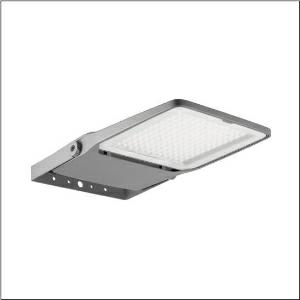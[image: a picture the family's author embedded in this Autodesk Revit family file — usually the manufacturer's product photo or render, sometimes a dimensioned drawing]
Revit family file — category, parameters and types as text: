
# Revit family: floodlight_fl_20_midi___rs17_5xa7682d3b2ac_ca3f
name_source: partatom
category: Lighting Fixtures
units: mm (PartAtom-declared; Revit-internal decimal feet)

## family parameters
Cut with Voids When Loaded = No
Host = Face
Light Source = No
Part Type = Normal
Room Calculation Point = No
Round Connector Dimension = Use Diameter
Shared = No

## types (1)
- --- (1 x LED 5000K / CRI = 70 (unbekannt), 19830 lm, 5000K)
    Apparent Load = 142 VA
    CIE Flux Codes = 79 92 99 100 100
    Color Rendering = 70
    Color Temperature = 5000K
    Default Elevation = 1800 mm
    Description = Floodlight FL 20 midi, floodlight, primary light control with lens, of plastic, primary optical cover: protective disc, of toughened safety glass, transparent, light distribution: RS17, light emission: direct distribution, primary light characteristic: rotationally symmetric, installation type: surface-mounted, LED High Power LED, rated luminous flux: 19.830 lm, light colour: 750, colour temperature: 5000K, control gear: ECG Plus, control: flexible luminous flux parameterisation, time-dependent luminous flux control, digital communication interface, power reduction, overheat protection, electronic power reduction, with terminal, 5-pole, max. 2.5mm², mains connection: 220..240V, AC, 50/60Hz, rated input power: 142W, LED unit, of diecast aluminium, powder-coated, Siteco® metallic grey (DB 702S), length: 731 mm, width: 450 mm, height: 76mm, housing frame, of diecast aluminium, powder-coated, Siteco® metallic grey (DB 702S), wall fastening, of steel, powder-coated, Siteco® metallic grey (DB 702S), DALIprotection rating (complete): IP66, insulation class (complete): insulation class II (safety insulation), certification: CE, ENEC, VDE, protection symbol: D, permissible ambient temperature for indoor applications: -40..+40°C, permissible ambient temperature for outdoor applications: -40..+50°C, standard: DIN EN 12944, packaging unit: 1 piece

Light Distribution: RS17
    Height = 76 mm
    Lamp = 1 x LED 5000K / CRI >= 70 (unbekannt)
    Lamp Light Flux = 19830 lm
    Lamp count = 1
    Length = 731 mm
    Luminous efficacy = 140 lm/W
    Manufacturer = Siteco
    ModVariant = No
    Model = 5XA7682D3B2AC
    Number of Poles = 1
    OnlyDefault = Yes
    Power Factor = 1
    Product Name = Floodlight FL 20 midi | RS17
    Product group = floodlight | pylon top
    ProductGroupID = 6101
    Protection Class = Protection class II
    Protection Degree = IP 66
    RLX_Detail_Level = 1
    RlxData = <blob elided: 86645 chars, md5=422145df>
    Socket = socket
    Standby Power = 0 W
    System Light Flux = 19830 lm
    System Power = 142 W
    Type Comments = factory setting: luminous flux: 100 % | dim-lin: 254 | 489 mA
    Type Image = l_1005944.jpg
    URL = http://relux.com
    VarID = @adj_141921
    Voltage = 0 V
    Weight = 0.00 kg
    Width = 450 mm

## geometry (parser evidence)
native form markers: Blend x4, Sweep x13
no freeform markers — native parametric forms only
